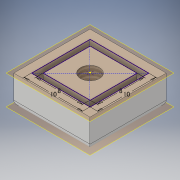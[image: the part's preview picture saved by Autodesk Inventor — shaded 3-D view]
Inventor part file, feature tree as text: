
AUTODESK INVENTOR PART (.ipt)
format: ipt  version: 2019.3 (Build 233278000, 278)  size: 129,024 bytes
history: native  units: in
note: dims shown in document units (in); Inventor stores cm internally (conversion verified against a paired STEP export)
features: sketch x4, extrude x2, other x1, hole x1, fillet x1
ambient origin geometry x8: Origin, YZ Plane, XZ Plane, XY Plane, X Axis, Y Axis, Z Axis, Center Point
bodies: Body1 (feature_tree)
feature tree (9):
  extrude  "押し出し4"  Depth=0.5118in
  other  "作業平面2"
  sketch  "スケッチ3"
  extrude  "押し出し5"  Depth=0.5118in
  hole  "穴1"  [1 undecoded]
  fillet  "フィレット1"  Radius=0.1969in
  sketch  "スケッチ4"
  sketch  "スケッチ5"
  sketch  "スケッチ1"
note: 1 required parameter value undecoded (feature->parameter linkage not recoverable at this tier; creation-order binding heuristic only, values carry confidence <= 0.55)
